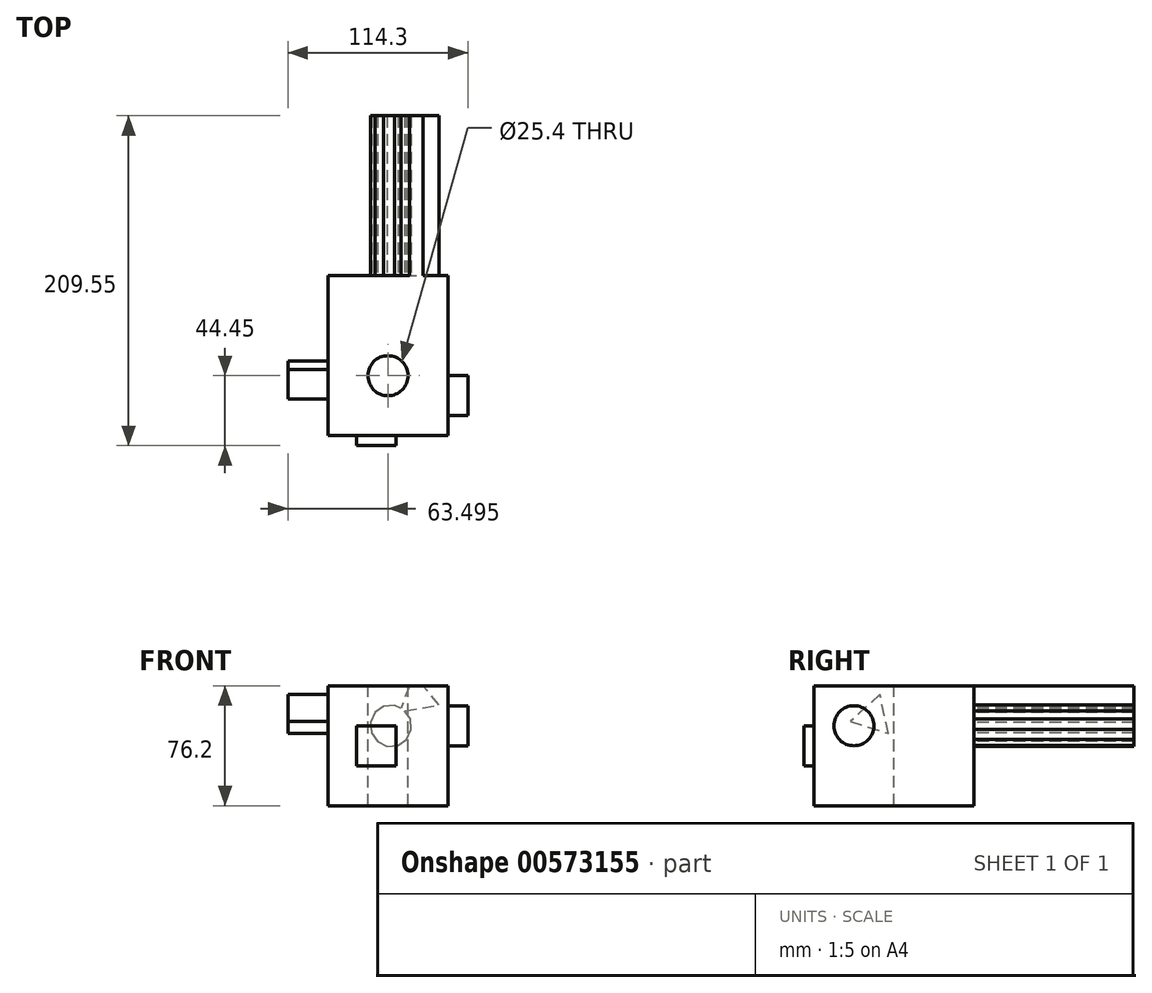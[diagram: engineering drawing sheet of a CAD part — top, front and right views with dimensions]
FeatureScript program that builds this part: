
annotation { "Feature Type Name" : "Feature", "Feature Type Description" : "" }
export const myFeature = defineFeature(function(context is Context, id is Id, definition is map)
    precondition{}
    {
        {
            var Q0;
            Q0=qCreatedBy(makeId("Front.planeOp"),FACE);
            var sketch = newSketch(context, id + "F0", { "sketchPlane" : qUnion([Q0])});
            skLineSegment(sketch, "E0.bottom", {"start": v(-75.06, 77.85) * mm, "end": v(1.14, 77.85) * mm});
            skLineSegment(sketch, "E0.top", {"start": v(-75.06, 1.65) * mm, "end": v(1.14, 1.65) * mm});
            skLineSegment(sketch, "E0.left", {"start": v(-75.06, 77.85) * mm, "end": v(-75.06, 1.65) * mm});
            skLineSegment(sketch, "E0.right", {"start": v(1.14, 77.85) * mm, "end": v(1.14, 1.65) * mm});
            skSolve(sketch);
        }
        {
            var Q0;
            Q0=makeQuery(id+"F0.imprint","IMPRINT",FACE,{"disambiguationData":[TD([[makeQuery(id+"F0.imprint","IMPRINT",EDGE,{"derivedFrom":sQuery(id+"F0.wireOp",EDGE,"E0.bottom")}),-1.0]])]});
            extrude(context, id + "F1", {"entities" : qUnion([Q0]), "depth" : 76.2 * mm, "offsetDistance" : 25.4 * mm});
        }
        {
            var Q0;
            Q0=makeQuery(id+"F1.opExtrude","CAP_FACE",FACE,{"disambiguationData":[OSD([sQuery(id+"F0.wireOp",EDGE,"E0.bottom"),sQuery(id+"F0.wireOp",EDGE,"E0.top"),sQuery(id+"F0.wireOp",EDGE,"E0.left"),sQuery(id+"F0.wireOp",EDGE,"E0.right")])],"isStart":false});
            var sketch = newSketch(context, id + "F2", { "sketchPlane" : qUnion([Q0])});
            skLineSegment(sketch, "E1.bottom", {"start": v(-57.05, 52.45) * mm, "end": v(-31.65, 52.45) * mm});
            skLineSegment(sketch, "E1.top", {"start": v(-57.05, 27.05) * mm, "end": v(-31.65, 27.05) * mm});
            skLineSegment(sketch, "E1.left", {"start": v(-57.05, 52.45) * mm, "end": v(-57.05, 27.05) * mm});
            skLineSegment(sketch, "E1.right", {"start": v(-31.65, 52.45) * mm, "end": v(-31.65, 27.05) * mm});
            skSolve(sketch);
        }
        {
            var Q0;
            Q0=makeQuery(id+"F2.imprint","IMPRINT",FACE,{"disambiguationData":[TD([[makeQuery(id+"F2.imprint","IMPRINT",EDGE,{"derivedFrom":sQuery(id+"F2.wireOp",EDGE,"E1.bottom")}),-1.0]])]});
            extrude(context, id + "F3", {"entities" : qUnion([Q0]), "operationType" : NewBodyOperationType.ADD, "depth" : 6.35 * mm, "offsetDistance" : 25.4 * mm});
        }
        {
            var Q0;
            Q0=makeQuery(id+"F1.opExtrude","SWEPT_FACE",FACE,{"disambiguationData":[OSD([sQuery(id+"F0.wireOp",EDGE,"E0.right")])]});
            var sketch = newSketch(context, id + "F4", { "sketchPlane" : qUnion([Q0])});
            skCircle(sketch, "E2", {"center": v(-50.8, 52.45) * mm, "radius": 12.7 * mm});
            skSolve(sketch);
        }
        {
            var Q0;
            Q0=makeQuery(id+"F4.imprint","IMPRINT",FACE,{"disambiguationData":[TD([[makeQuery(id+"F4.imprint","IMPRINT",EDGE,{"derivedFrom":sQuery(id+"F4.wireOp",EDGE,"E2")}),1.0]])]});
            extrude(context, id + "F5", {"entities" : qUnion([Q0]), "operationType" : NewBodyOperationType.ADD, "depth" : 12.7 * mm, "offsetDistance" : 25.4 * mm});
        }
        {
            var Q0;
            Q0=makeQuery(id+"F1.opExtrude","SWEPT_FACE",FACE,{"disambiguationData":[OSD([sQuery(id+"F0.wireOp",EDGE,"E0.bottom")])]});
            var sketch = newSketch(context, id + "F6", { "sketchPlane" : qUnion([Q0])});
            skPoint(sketch, "E3", {"position": v(-36.96, -38.1) * mm});
            skSolve(sketch);
        }
        {
            var Q0;
            Q0=sQuery(id+"F6.wireOp",VERTEX,"E3");
            var Q1;
            Q1=makeQuery(id+"F1.opExtrude","SWEPT_BODY",BODY,{"disambiguationData":[OSD([sQuery(id+"F0.wireOp",EDGE,"E0.bottom"),sQuery(id+"F0.wireOp",EDGE,"E0.top"),sQuery(id+"F0.wireOp",EDGE,"E0.left"),sQuery(id+"F0.wireOp",EDGE,"E0.right")])]});
            hole(context, id + "F7", {"style" : HoleStyle.SIMPLE, "endStyle" : HoleEndStyle.THROUGH, "holeDiameter" : 25.4 * mm, "isTappedThrough" : true, "tappedDepth" : 12.7 * mm, "tapClearance" : 3, "locations" : qUnion([Q0]), "scope" : qUnion([Q1])});
        }
        {
            var Q0;
            Q0=makeQuery(id+"F1.opExtrude","SWEPT_FACE",FACE,{"disambiguationData":[OSD([sQuery(id+"F0.wireOp",EDGE,"E0.left")])]});
            var sketch = newSketch(context, id + "F8", { "sketchPlane" : qUnion([Q0])});
            skCircle(sketch, "E4.cCircle", {"center": v(38.68, 58.38) * mm, "radius": 7.33 * mm, "construction": true});
            skLineSegment(sketch, "E4.0", {"start": v(53, 55.2) * mm, "end": v(28.78, 47.56) * mm});
            skLineSegment(sketch, "E4.1", {"start": v(28.78, 47.56) * mm, "end": v(34.27, 72.36) * mm});
            skLineSegment(sketch, "E4.2", {"start": v(34.27, 72.36) * mm, "end": v(53, 55.2) * mm});
            skPoint(sketch, "E4.0.midPoint", {"position": v(40.89, 51.38) * mm});
            skSolve(sketch);
        }
        {
            var Q0;
            Q0=makeQuery(id+"F8.imprint","IMPRINT",FACE,{"disambiguationData":[TD([[makeQuery(id+"F8.imprint","IMPRINT",EDGE,{"derivedFrom":sQuery(id+"F8.wireOp",EDGE,"E4.0")}),-1.0]])]});
            extrude(context, id + "F9", {"entities" : qUnion([Q0]), "operationType" : NewBodyOperationType.ADD, "depth" : 25.4 * mm, "offsetDistance" : 25.4 * mm});
        }
        {
            var Q0;
            Q0=makeQuery(id+"F1.opExtrude","CAP_FACE",FACE,{"disambiguationData":[OSD([sQuery(id+"F0.wireOp",EDGE,"E0.bottom"),sQuery(id+"F0.wireOp",EDGE,"E0.top"),sQuery(id+"F0.wireOp",EDGE,"E0.left"),sQuery(id+"F0.wireOp",EDGE,"E0.right")])],"isStart":true});
            var sketch = newSketch(context, id + "F10", { "sketchPlane" : qUnion([Q0])});
            skCircle(sketch, "E5.cCircle", {"center": v(35.13, 52.4) * mm, "radius": 70.76 * mm, "construction": true});
            skLineSegment(sketch, "E5.0", {"start": v(119.48, 29.27) * mm, "end": v(39.19, -34.96) * mm});
            skLineSegment(sketch, "E5.1", {"start": v(39.19, -34.96) * mm, "end": v(-46.7, 21.55) * mm});
            skLineSegment(sketch, "E5.2", {"start": v(-46.7, 21.55) * mm, "end": v(-19.5, 120.7) * mm});
            skLineSegment(sketch, "E5.3", {"start": v(-19.5, 120.7) * mm, "end": v(83.2, 125.47) * mm});
            skLineSegment(sketch, "E5.4", {"start": v(83.2, 125.47) * mm, "end": v(119.48, 29.27) * mm});
            skPoint(sketch, "E5.0.midPoint", {"position": v(79.33, -2.85) * mm});
            skCircle(sketch, "E6.cCircle", {"center": v(35.13, 52.4) * mm, "radius": 12.7 * mm, "construction": true});
            skLineSegment(sketch, "E6.0", {"start": v(47.5, 47.94) * mm, "end": v(43.6, 42.35) * mm});
            skLineSegment(sketch, "E6.1", {"start": v(43.6, 42.35) * mm, "end": v(37.44, 39.46) * mm});
            skLineSegment(sketch, "E6.2", {"start": v(37.44, 39.46) * mm, "end": v(30.66, 40.04) * mm});
            skLineSegment(sketch, "E6.3", {"start": v(30.66, 40.04) * mm, "end": v(25.08, 43.93) * mm});
            skLineSegment(sketch, "E6.4", {"start": v(25.08, 43.93) * mm, "end": v(22.19, 50.1) * mm});
            skLineSegment(sketch, "E6.5", {"start": v(22.19, 50.1) * mm, "end": v(22.77, 56.88) * mm});
            skLineSegment(sketch, "E6.6", {"start": v(22.77, 56.88) * mm, "end": v(26.66, 62.46) * mm});
            skLineSegment(sketch, "E6.7", {"start": v(26.66, 62.46) * mm, "end": v(32.82, 65.35) * mm});
            skLineSegment(sketch, "E6.8", {"start": v(32.82, 65.35) * mm, "end": v(39.6, 64.77) * mm});
            skLineSegment(sketch, "E6.9", {"start": v(39.6, 64.77) * mm, "end": v(45.18, 60.88) * mm});
            skLineSegment(sketch, "E6.10", {"start": v(45.18, 60.88) * mm, "end": v(48.07, 54.72) * mm});
            skLineSegment(sketch, "E6.11", {"start": v(48.07, 54.72) * mm, "end": v(47.5, 47.94) * mm});
            skPoint(sketch, "E6.0.midPoint", {"position": v(45.55, 45.14) * mm});
            skCircle(sketch, "E7.cCircle", {"center": v(-7.12, 121.28) * mm, "radius": 17.97 * mm, "construction": true});
            skLineSegment(sketch, "E7.0", {"start": v(28.35, 115.44) * mm, "end": v(-29.91, 93.47) * mm});
            skLineSegment(sketch, "E7.1", {"start": v(-29.91, 93.47) * mm, "end": v(-19.8, 154.91) * mm});
            skLineSegment(sketch, "E7.2", {"start": v(-19.8, 154.91) * mm, "end": v(28.35, 115.44) * mm});
            skPoint(sketch, "E7.0.midPoint", {"position": v(-0.78, 104.46) * mm});
            skCircle(sketch, "E8.cCircle", {"center": v(18.22, 70.7) * mm, "radius": 7.33 * mm, "construction": true});
            skLineSegment(sketch, "E8.0", {"start": v(20.6, 85.17) * mm, "end": v(29.56, 61.4) * mm});
            skLineSegment(sketch, "E8.1", {"start": v(29.56, 61.4) * mm, "end": v(4.5, 65.53) * mm});
            skLineSegment(sketch, "E8.2", {"start": v(4.5, 65.53) * mm, "end": v(20.6, 85.17) * mm});
            skPoint(sketch, "E8.0.midPoint", {"position": v(25.08, 73.3) * mm});
            skSolve(sketch);
        }
        {
            var Q0;
            Q0=makeQuery(id+"F10.imprint","IMPRINT",FACE,{"disambiguationData":[TD([[makeQuery(id+"F10.imprint","IMPRINT",EDGE,{"derivedFrom":sQuery(id+"F10.wireOp",EDGE,"E6.0")}),1.0]])]});
            extrude(context, id + "F11", {"entities" : qUnion([Q0]), "operationType" : NewBodyOperationType.ADD, "depth" : 25.4 * mm, "offsetDistance" : 25.4 * mm});
        }
        {
            var Q0;
            Q0=makeQuery(id+"F1.opExtrude","CAP_FACE",FACE,{"disambiguationData":[OSD([sQuery(id+"F0.wireOp",EDGE,"E0.bottom"),sQuery(id+"F0.wireOp",EDGE,"E0.top"),sQuery(id+"F0.wireOp",EDGE,"E0.left"),sQuery(id+"F0.wireOp",EDGE,"E0.right")])],"isStart":true});
            extrude(context, id + "F12", {"entities" : qUnion([Q0]), "operationType" : NewBodyOperationType.ADD, "depth" : 127 * mm, "offsetDistance" : 25.4 * mm});
        }
    });
